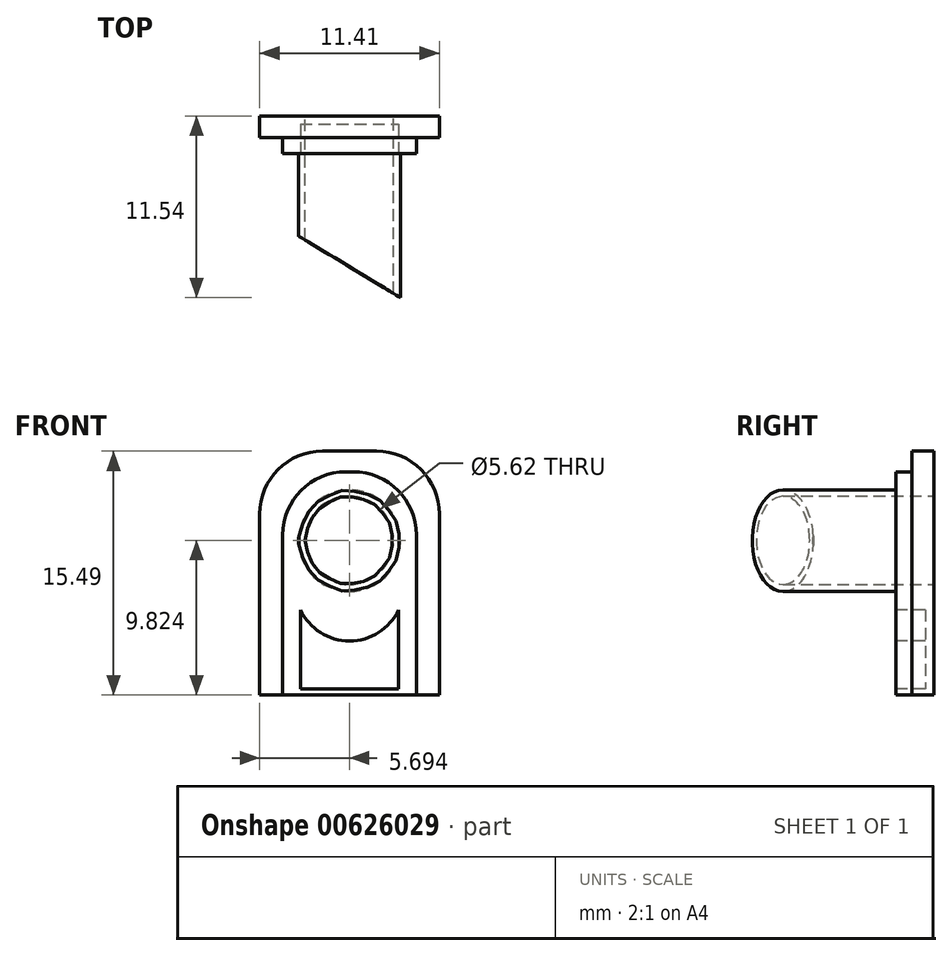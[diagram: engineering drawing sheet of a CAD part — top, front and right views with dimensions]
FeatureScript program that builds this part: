
annotation { "Feature Type Name" : "Feature", "Feature Type Description" : "" }
export const myFeature = defineFeature(function(context is Context, id is Id, definition is map)
    precondition{}
    {
        {
            var Q0;
            Q0=qCreatedBy(makeId("Front.planeOp"),FACE);
            var sketch = newSketch(context, id + "F0", { "sketchPlane" : qUnion([Q0])});
            skLineSegment(sketch, "E0", {"start": v(-4.65, -3.16) * mm, "end": v(6.76, -3.16) * mm});
            skLineSegment(sketch, "E1", {"start": v(6.76, -3.16) * mm, "end": v(6.76, 12.33) * mm});
            skLineSegment(sketch, "E2", {"start": v(6.76, 12.33) * mm, "end": v(-4.65, 12.33) * mm});
            skLineSegment(sketch, "E3", {"start": v(-4.65, 12.33) * mm, "end": v(-4.65, -3.16) * mm});
            skSolve(sketch);
        }
        {
            var Q0;
            Q0 = qSketchRegion(id + "F0", true);
            extrude(context, id + "F1", {"entities" : qUnion([Q0]), "depth" : 1.39 * mm, "offsetDistance" : 25 * mm});
        }
        {
            var Q0;
            Q0=makeQuery(id+"F1.opExtrude","CAP_FACE",FACE,{"disambiguationData":[OSD([sQuery(id+"F0.wireOp",EDGE,"E0"),sQuery(id+"F0.wireOp",EDGE,"E1"),sQuery(id+"F0.wireOp",EDGE,"E2"),sQuery(id+"F0.wireOp",EDGE,"E3")])],"isStart":false});
            var sketch = newSketch(context, id + "F2", { "sketchPlane" : qUnion([Q0])});
            skLineSegment(sketch, "E4", {"start": v(-3.18, -3.16) * mm, "end": v(-3.18, 11.01) * mm});
            skLineSegment(sketch, "E5", {"start": v(-3.18, 11.01) * mm, "end": v(5.3, 11.01) * mm});
            skLineSegment(sketch, "E6", {"start": v(5.3, 11.01) * mm, "end": v(5.3, -3.16) * mm});
            skLineSegment(sketch, "E7", {"start": v(5.3, -3.16) * mm, "end": v(-3.18, -3.16) * mm});
            skSolve(sketch);
        }
        {
            var Q0;
            Q0 = qSketchRegion(id + "F2", true);
            extrude(context, id + "F3", {"entities" : qUnion([Q0]), "operationType" : NewBodyOperationType.ADD, "depth" : 1 * mm, "offsetDistance" : 25 * mm});
        }
        {
            var Q0;
            Q0=makeQuery(id+"F3.opExtrude","CAP_FACE",FACE,{"disambiguationData":[OSD([sQuery(id+"F2.wireOp",EDGE,"E4"),sQuery(id+"F2.wireOp",EDGE,"E5"),sQuery(id+"F2.wireOp",EDGE,"E6"),sQuery(id+"F2.wireOp",EDGE,"E7")])],"isStart":false});
            var sketch = newSketch(context, id + "F4", { "sketchPlane" : qUnion([Q0])});
            skCircle(sketch, "E8", {"center": v(1.06, 6.64) * mm, "radius": 3.23 * mm});
            skSolve(sketch);
        }
        {
            var Q0;
            Q0 = qSketchRegion(id + "F4", true);
            extrude(context, id + "F5", {"entities" : qUnion([Q0]), "operationType" : NewBodyOperationType.ADD, "depth" : 9.16 * mm, "offsetDistance" : 25 * mm});
        }
        {
            var Q0;
            Q0=makeQuery(id+"F1.opExtrude","SWEPT_EDGE",EDGE,{"disambiguationData":[OSD([sQuery(id+"F0.wireOp",EDGE,"E2"),sQuery(id+"F0.wireOp",EDGE,"E3")])]});
            var Q1;
            Q1=makeQuery(id+"F1.opExtrude","SWEPT_EDGE",EDGE,{"disambiguationData":[OSD([sQuery(id+"F0.wireOp",EDGE,"E1"),sQuery(id+"F0.wireOp",EDGE,"E2")])]});
            var Q2;
            Q2=makeQuery(id+"F3.opExtrude","SWEPT_EDGE",EDGE,{"disambiguationData":[OSD([sQuery(id+"F2.wireOp",EDGE,"E5"),sQuery(id+"F2.wireOp",EDGE,"E6")])]});
            var Q3;
            Q3=makeQuery(id+"F3.opExtrude","SWEPT_EDGE",EDGE,{"disambiguationData":[OSD([sQuery(id+"F2.wireOp",EDGE,"E4"),sQuery(id+"F2.wireOp",EDGE,"E5")])]});
            fillet(context, id + "F6", {"entities" : qUnion([Q0, Q1, Q2, Q3]), "radius" : 4 * mm, "tangentPropagation" : true, "allowEdgeOverflow" : false});
        }
        {
            var Q0;
            Q0=qCreatedBy(makeId("Front.planeOp"),FACE);
            var sketch = newSketch(context, id + "F7", { "sketchPlane" : qUnion([Q0])});
            skCircle(sketch, "E9", {"center": v(1.04, 6.66) * mm, "radius": 2.8 * mm});
            skSolve(sketch);
        }
        {
            var Q0;
            Q0 = qSketchRegion(id + "F7", true);
            extrude(context, id + "F8", {"entities" : qUnion([Q0]), "operationType" : NewBodyOperationType.REMOVE, "endBound" : BoundingType.THROUGH_ALL, "depth" : 25 * mm, "offsetDistance" : 25 * mm});
        }
        {
            var Q0;
            Q0=qCreatedBy(makeId("Top.planeOp"),FACE);
            var sketch = newSketch(context, id + "F9", { "sketchPlane" : qUnion([Q0])});
            skLineSegment(sketch, "E10", {"start": v(-2.16, -7.64) * mm, "end": v(5.48, -12.26) * mm});
            skLineSegment(sketch, "E11", {"start": v(5.48, -12.26) * mm, "end": v(-4.16, -12.26) * mm});
            skLineSegment(sketch, "E12", {"start": v(-4.16, -12.26) * mm, "end": v(-2.16, -7.64) * mm});
            skSolve(sketch);
        }
        {
            var Q0;
            Q0 = qSketchRegion(id + "F9", true);
            extrude(context, id + "F10", {"entities" : qUnion([Q0]), "operationType" : NewBodyOperationType.REMOVE, "depth" : 25 * mm, "offsetDistance" : 25 * mm});
        }
        {
            var Q0;
            Q0=makeQuery(id+"F3.opExtrude","CAP_FACE",FACE,{"disambiguationData":[OSD([sQuery(id+"F2.wireOp",EDGE,"E4"),sQuery(id+"F2.wireOp",EDGE,"E5"),sQuery(id+"F2.wireOp",EDGE,"E6"),sQuery(id+"F2.wireOp",EDGE,"E7")])],"isStart":false});
            var sketch = newSketch(context, id + "F11", { "sketchPlane" : qUnion([Q0])});
            skLineSegment(sketch, "E13", {"start": v(-2.06, 2.25) * mm, "end": v(4.18, 2.25) * mm});
            skArc(sketch, "E14", {"start": v(-2.06, 2.25) * mm, "mid": v(1.06, 0.27) * mm, "end": v(4.18, 2.25) * mm});
            skLineSegment(sketch, "E15", {"start": v(-2.06, 2.25) * mm, "end": v(-2.06, -2.77) * mm});
            skLineSegment(sketch, "E16", {"start": v(-2.06, -2.77) * mm, "end": v(4.18, -2.77) * mm});
            skLineSegment(sketch, "E17", {"start": v(4.18, -2.77) * mm, "end": v(4.18, 2.25) * mm});
            skSolve(sketch);
        }
        {
            var Q0;
            Q0=makeQuery(id+"F11.imprint","IMPRINT",FACE,{"disambiguationData":[TD([[makeQuery(id+"F11.imprint","IMPRINT",EDGE,{"derivedFrom":sQuery(id+"F11.wireOp",EDGE,"E14")}),-1.0]])]});
            extrude(context, id + "F12", {"entities" : qUnion([Q0]), "operationType" : NewBodyOperationType.REMOVE, "oppositeDirection" : true, "depth" : 1.87 * mm, "offsetDistance" : 25 * mm});
        }
    });
